# Revit family: Bombito T
name_source: partatom
category: Мебель
revit_build: Autodesk Revit 2017 (Build: 20160225_1515(x64)
units: mm (PartAtom-declared; Revit-internal decimal feet)

## family parameters
Всегда вертикально = Да
Заголовок OmniClass = General Furniture and Specialties
На основе рабочей плоскости = Нет
Номер OmniClass = 23.40.20.00
Общий = Нет
При загрузке вырезать с полостями = Нет
Точка расчета площади = Нет

## types (6) — shared parameters
Leg = Skandiform Chrome
Seat = Skandiform Fabric
Изготовитель = Skandiform AB
Ключевая пометка = XBF.2
Комментарии к типоразмеру = Created by Astacus AB

## per-type parameters (varying)
| type | Chair Legs | Chair Seat | URL | Описание |
| KS-139 | Leg-arm | 39 | http://www.biminfo.se | S-038 and KS-138 in birch, stained as option. S-039 and KS-139 are upholstered.
Chassis in chromium or silver lacquered metal.
Underrede i krom eller silverlackerad metall. /
S-058 and KS-158 in birch, stained as option. S-059 and KS-159 are upholstered.
Underframe in chromium or silver lacquered metal.
Bar stool in black laminate K1015UN. Chassis in chromium. |
| KS-138 | Leg-arm | 38 | http://www.biminfo.se | S-038 and KS-138 in birch, stained as option. S-039 and KS-139 are upholstered.
Chassis in chromium or silver lacquered metal. |
| S-038 | Leg | 38 | http://www.biminfo.se | S-038 and KS-138 in birch, stained as option. S-039 and KS-139 are upholstered.
Chassis in chromium or silver lacquered metal. |
| S-039 | Leg | 39 | http://www.biminfo.se | S-038 and KS-138 in birch, stained as option. S-039 and KS-139 are upholstered.
Chassis in chromium or silver lacquered metal. |
| KS-179 | Leg-arm | 39 | http://www.biminfo.se | S-038 and KS-138 in birch, stained as option. S-039 and KS-139 are upholstered.
Chassis in chromium or silver lacquered metal. |
| S-079 | Leg | 79 | http://file-system.ru | S-038 and KS-138 in birch, stained as option. S-039 and KS-139 are upholstered.
Chassis in chromium or silver lacquered metal. |

note: column(s) folded — value = type name in every type: Группа модели

## geometry (parser evidence)
native form markers: Blend x19, Sweep x12
no freeform markers — native parametric forms only
